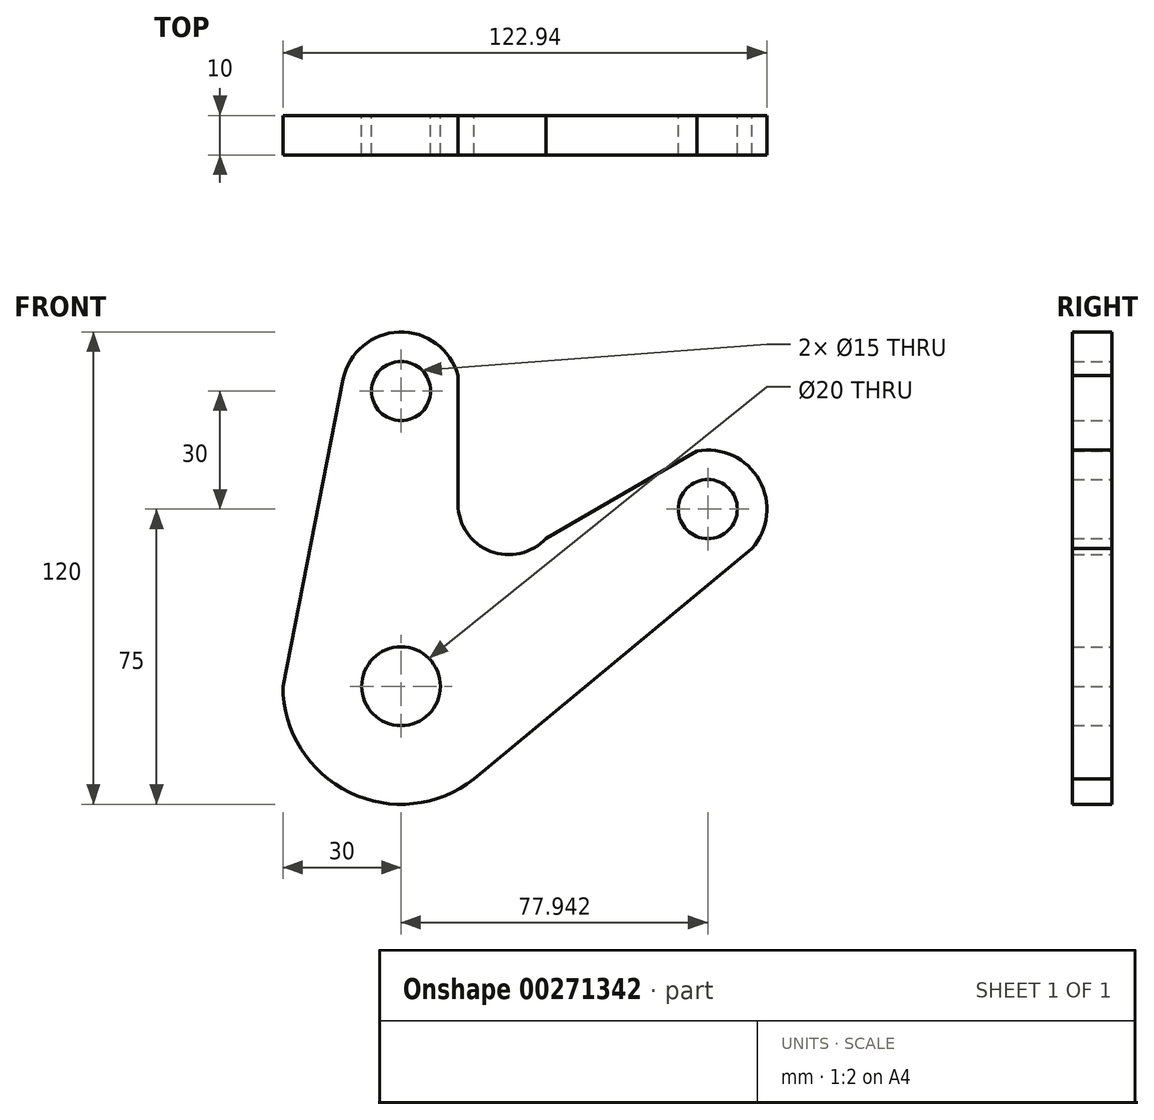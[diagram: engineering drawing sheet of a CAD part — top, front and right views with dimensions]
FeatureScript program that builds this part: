
annotation { "Feature Type Name" : "Feature", "Feature Type Description" : "" }
export const myFeature = defineFeature(function(context is Context, id is Id, definition is map)
    precondition{}
    {
        {
            var Q0;
            Q0=qCreatedBy(makeId("Front.planeOp"),FACE);
            var sketch = newSketch(context, id + "F0", { "sketchPlane" : qUnion([Q0])});
            skCircle(sketch, "E0", {"center": v(0, 0) * mm, "radius": 10 * mm});
            skArc(sketch, "E1", {"start": v(-30, 0) * mm, "mid": v(-13.13, -26.97) * mm, "end": v(18.5, -23.61) * mm});
            skCircle(sketch, "E2", {"center": v(77.94, 45) * mm, "radius": 7.5 * mm});
            skCircle(sketch, "E3", {"center": v(0, 75) * mm, "radius": 7.5 * mm});
            skArc(sketch, "E4", {"start": v(14.47, 78.94) * mm, "mid": v(-0.47, 90) * mm, "end": v(-14.7, 78.03) * mm});
            skArc(sketch, "E5", {"start": v(89.1, 34.97) * mm, "mid": v(91.03, 52.33) * mm, "end": v(75.22, 59.75) * mm});
            skLineSegment(sketch, "E6", {"start": v(-30, 0) * mm, "end": v(-14.7, 78.03) * mm});
            skLineSegment(sketch, "E7", {"start": v(18.5, -23.61) * mm, "end": v(89.1, 34.97) * mm});
            skLineSegment(sketch, "E8", {"start": v(14.47, 78.94) * mm, "end": v(14.47, 46.28) * mm});
            skLineSegment(sketch, "E9", {"start": v(0, 75) * mm, "end": v(0, 0) * mm, "construction": true});
            skLineSegment(sketch, "E10", {"start": v(0, 0) * mm, "end": v(77.94, 45) * mm, "construction": true});
            skLineSegment(sketch, "E11", {"start": v(75.22, 59.75) * mm, "end": v(36.83, 37.58) * mm});
            skArc(sketch, "E12", {"start": v(14.47, 46.28) * mm, "mid": v(22.68, 34.29) * mm, "end": v(36.83, 37.58) * mm});
            skSolve(sketch);
        }
        {
            var Q0;
            Q0 = qSketchRegion(id + "F0", true);
            extrude(context, id + "F1", {"entities" : qUnion([Q0]), "depth" : 10 * mm});
        }
    });
